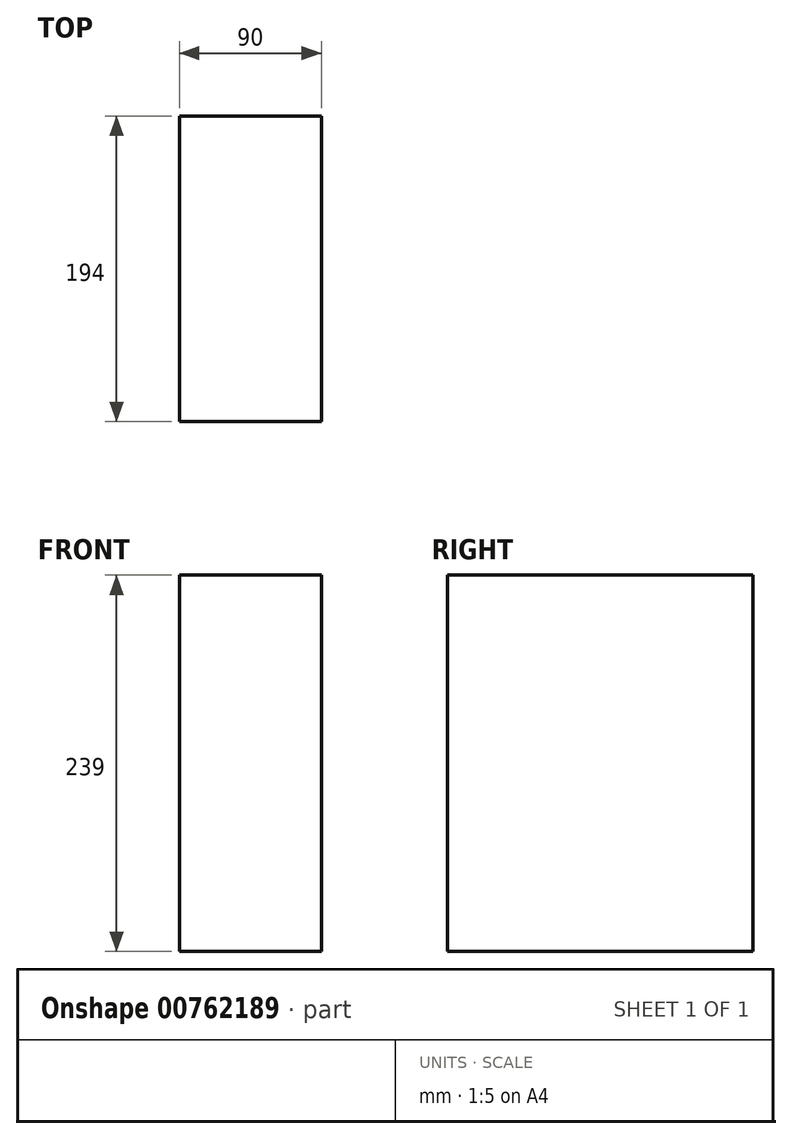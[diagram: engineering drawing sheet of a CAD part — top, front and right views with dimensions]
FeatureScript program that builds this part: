
annotation { "Feature Type Name" : "Feature", "Feature Type Description" : "" }
export const myFeature = defineFeature(function(context is Context, id is Id, definition is map)
    precondition{}
    {
        {
            var Q0;
            Q0=qCreatedBy(makeId("Front.planeOp"),FACE);
            var sketch = newSketch(context, id + "F0", { "sketchPlane" : qUnion([Q0])});
            skLineSegment(sketch, "E0.bottom", {"start": v(-45, 119.5) * mm, "end": v(45, 119.5) * mm});
            skLineSegment(sketch, "E0.top", {"start": v(-45, -119.5) * mm, "end": v(45, -119.5) * mm});
            skLineSegment(sketch, "E0.left", {"start": v(-45, 119.5) * mm, "end": v(-45, -119.5) * mm});
            skLineSegment(sketch, "E0.right", {"start": v(45, 119.5) * mm, "end": v(45, -119.5) * mm});
            skPoint(sketch, "E0.middle", {"position": v(0, 0) * mm});
            skSolve(sketch);
        }
        {
            var Q0;
            Q0=makeQuery(id+"F0.imprint","IMPRINT",FACE,{"disambiguationData":[TD([[makeQuery(id+"F0.imprint","IMPRINT",EDGE,{"derivedFrom":sQuery(id+"F0.wireOp",EDGE,"E0.bottom")}),-1.0]])]});
            extrude(context, id + "F1", {"entities" : qUnion([Q0]), "endBound" : BoundingType.SYMMETRIC, "depth" : 194 * mm, "offsetDistance" : 25 * mm});
        }
    });
